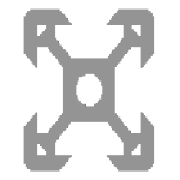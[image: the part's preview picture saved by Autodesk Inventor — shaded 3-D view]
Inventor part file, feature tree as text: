
AUTODESK INVENTOR PART (.ipt)
format: ipt  version: 2019 (Build 230136000, 136)  size: 200,192 bytes
history: native  units: mm
features: other x3, sketch x3, plane x1
ambient origin geometry x8: Origin, YZ Plane, XZ Plane, XY Plane, X Axis, Y Axis, Z Axis, Center Point
bodies: Solid1 (feature_tree), Body (feature_tree)
feature tree (7):
  other  "Driven Length"
  other  "Start Plane"
  other  "End Plane"
  sketch  "Sketch1"  dims[d2=4.2mm]
  sketch  "Sketch4"  dims[d3=1.5mm]
  plane  "Work Plane4"
  sketch  "Sketch5"  dims[d4=1.64mm d5=1.8mm d6=5.68mm d7=1.8mm d9=1.5mm d12=-0.0mm d13=470.0mm d14=0.13mm d15=0.0mm d18=90.0deg d17=470.0mm]
